# Revit family: Shower-Digital_Interface-KOHLER-AIRFOIL-K-881T_1
name_source: partatom
category: Specialty Equipment
revit_build: Autodesk Revit 2017 (Build: 20160225_1515(x64)
units: mm (PartAtom-declared; Revit-internal decimal feet)

## family parameters
Cut with Voids When Loaded = No
Host = Face
OmniClass Number = 23.31.25.00
OmniClass Title = Toilet and Bath Specialties
Part Type = Normal
Room Calculation Point = No
Round Connector Dimension = Use Diameter
Shared = No

## types (1)
- CP-Polished Chrome
    ADA Compliant = No
    Apparent Load = 240 VA
    Assembly Code = C1030200
    Date Modified = 03/10/2021
    Default Elevation = 42"
    Description = XINYUE DTV constant temperature digital control panel
    Electrical Connector = Yes
    Electrical Note = One Dedicated Circuit Required
    Finish = Kohler-Plastic-CP-Polished_Chrome
    Height = 8 11/16"
    Length = 11/16"
    Manufacturer = KOHLER Co.
    Master Format 2014 = 10 28 00
    Master Format 2014 Name = Toilet, Bath, and Laundry Accessories
    Material = Plastic
    Model = K-881T-CP
    Product Documentation Link = https://files.kohler.com.cn
    Product Name = AIRFOIL
    Product Page URL = https://www.kohler.com.cn
    Type = 1
    URL = http://www.kohler.com.cn
    Voltage = 120 V
    WaterSense Certified = No
    Width = 3 9/16"

## geometry (parser evidence)
native form markers: Sweep x5
no freeform markers — native parametric forms only
